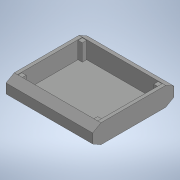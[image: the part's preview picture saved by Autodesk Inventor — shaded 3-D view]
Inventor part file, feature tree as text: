
AUTODESK INVENTOR PART (.ipt)
format: ipt  version: 2020 (Build 240168000, 168)  size: 159,744 bytes
history: native  units: in
note: dims shown in document units (in); Inventor stores cm internally (conversion verified against a paired STEP export)
features: extrude x3, sketch x3, projected_geometry x3
ambient origin geometry x8: Origin, YZ Plane, XZ Plane, XY Plane, X Axis, Y Axis, Z Axis, Center Point
bodies: Solid1 (feature_tree)
feature tree (9):
  extrude  "Extrusion1"  Depth=5.9055in
  extrude  "Extrusion2"  TaperAngle=0.0deg  [1 undecoded]
  extrude  "Extrusion3"  Depth=1.2598in
  sketch  "Sketch1"  dims[d0=1.378in d1=5.9055in]
  sketch  "Sketch2"  dims[d2=6.2992in d3=0.0in]
  projected_geometry  "Projected Loop1"
  sketch  "Sketch3"  dims[d4=0.2362in d5=1.2598in d6=0.0in d8=0.315in d10=1.2205in d11=0.0in]
  projected_geometry  "Projected Loop2"
  projected_geometry  "Projected Loop3"
note: 1 required parameter value undecoded (feature->parameter linkage not recoverable at this tier; creation-order binding heuristic only, values carry confidence <= 0.55)
